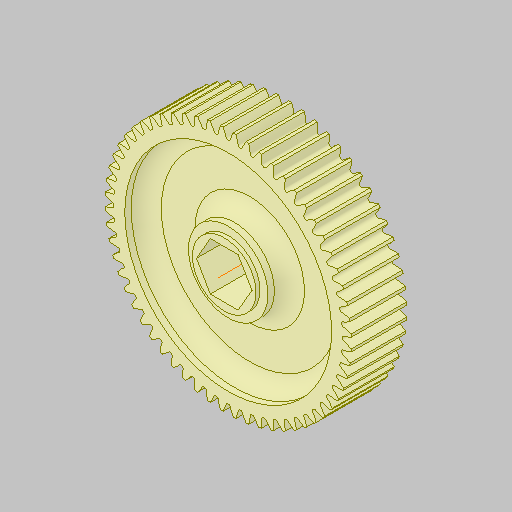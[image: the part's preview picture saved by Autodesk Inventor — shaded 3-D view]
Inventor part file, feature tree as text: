
AUTODESK INVENTOR PART (.ipt)
format: ipt  version: 2023.5 (Build 275446000, 446)  size: 657,920 bytes
history: native  units: in
note: dims shown in document units (in); Inventor stores cm internally (conversion verified against a paired STEP export)
features: mirror x1
ambient origin geometry x8: Origin, YZ Plane, XZ Plane, XY Plane, X Axis, Y Axis, Z Axis, Center Point
bodies: Solid1 (feature_tree)
feature tree (1):
  mirror  "Mirror1"
